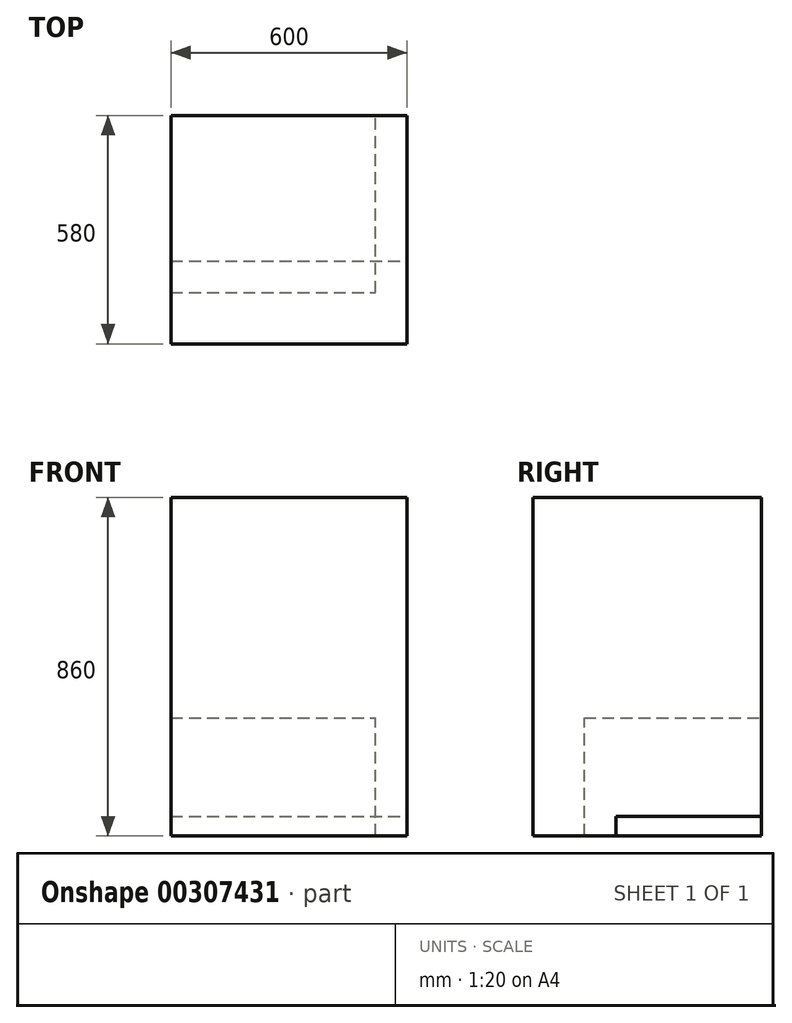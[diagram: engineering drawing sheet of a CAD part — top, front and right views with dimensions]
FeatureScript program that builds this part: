
annotation { "Feature Type Name" : "Feature", "Feature Type Description" : "" }
export const myFeature = defineFeature(function(context is Context, id is Id, definition is map)
    precondition{}
    {
        {
            var Q0;
            Q0=qCreatedBy(makeId("Front.planeOp"),FACE);
            var sketch = newSketch(context, id + "F0", { "sketchPlane" : qUnion([Q0])});
            skLineSegment(sketch, "E0.bottom", {"start": v(0, 0) * mm, "end": v(600, 0) * mm});
            skLineSegment(sketch, "E0.top", {"start": v(0, 860) * mm, "end": v(600, 860) * mm});
            skLineSegment(sketch, "E0.left", {"start": v(0, 0) * mm, "end": v(0, 860) * mm});
            skLineSegment(sketch, "E0.right", {"start": v(600, 0) * mm, "end": v(600, 860) * mm});
            skSolve(sketch);
        }
        {
            var Q0;
            Q0=makeQuery(id+"F0.imprint","IMPRINT",FACE,{"disambiguationData":[TD([[makeQuery(id+"F0.imprint","IMPRINT",EDGE,{"derivedFrom":sQuery(id+"F0.wireOp",EDGE,"E0.bottom")}),1.0]])]});
            extrude(context, id + "F1", {"entities" : qUnion([Q0]), "depth" : 580 * mm, "offsetDistance" : 25 * mm});
        }
        {
            var Q0;
            Q0=qCreatedBy(makeId("Front.planeOp"),FACE);
            var sketch = newSketch(context, id + "F2", { "sketchPlane" : qUnion([Q0])});
            skLineSegment(sketch, "E1.bottom", {"start": v(0, 0) * mm, "end": v(520, 0) * mm});
            skLineSegment(sketch, "E1.top", {"start": v(0, 300) * mm, "end": v(520, 300) * mm});
            skLineSegment(sketch, "E1.left", {"start": v(0, 0) * mm, "end": v(0, 300) * mm});
            skLineSegment(sketch, "E1.right", {"start": v(520, 0) * mm, "end": v(520, 300) * mm});
            skSolve(sketch);
        }
        {
            var Q0;
            Q0 = qSketchRegion(id + "F2", true);
            extrude(context, id + "F3", {"entities" : qUnion([Q0]), "depth" : 450 * mm, "offsetDistance" : 25 * mm});
        }
        {
            var Q0;
            Q0=qCreatedBy(makeId("Front.planeOp"),FACE);
            var sketch = newSketch(context, id + "F4", { "sketchPlane" : qUnion([Q0])});
            skLineSegment(sketch, "E2.0", {"start": v(0, 0) * mm, "end": v(0, 50) * mm});
            skLineSegment(sketch, "E3.0", {"start": v(0, 0) * mm, "end": v(600, 0) * mm});
            skLineSegment(sketch, "E4.0", {"start": v(600, 0) * mm, "end": v(600, 50) * mm});
            skLineSegment(sketch, "E5", {"start": v(0, 50) * mm, "end": v(600, 50) * mm});
            skPoint(sketch, "E6.orphan", {"position": v(0, 860) * mm});
            skPoint(sketch, "E7.orphan", {"position": v(600, 860) * mm});
            skSolve(sketch);
        }
        {
            var Q0;
            Q0 = qSketchRegion(id + "F4", true);
            extrude(context, id + "F5", {"entities" : qUnion([Q0]), "depth" : 370 * mm, "offsetDistance" : 25 * mm});
        }
    });
